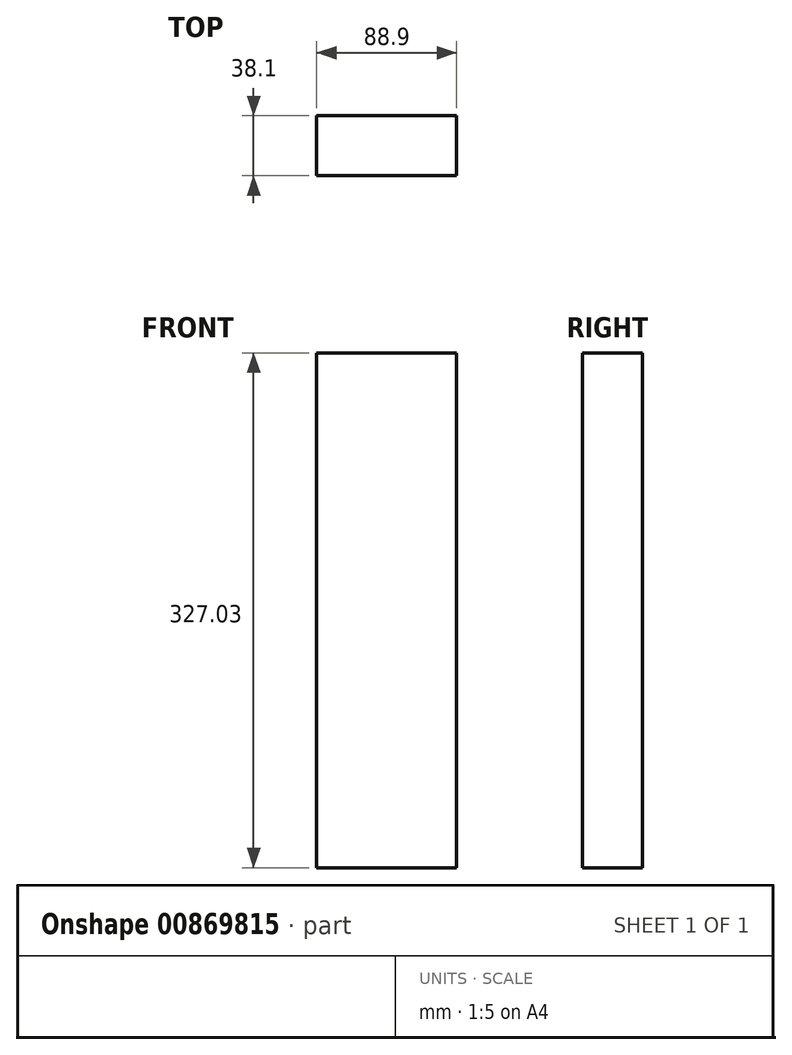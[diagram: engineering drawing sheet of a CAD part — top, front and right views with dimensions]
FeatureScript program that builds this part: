
annotation { "Feature Type Name" : "Feature", "Feature Type Description" : "" }
export const myFeature = defineFeature(function(context is Context, id is Id, definition is map)
    precondition{}
    {
        {
            var Q0;
            Q0=qCreatedBy(makeId("Top.planeOp"),FACE);
            var sketch = newSketch(context, id + "F0", { "sketchPlane" : qUnion([Q0])});
            skLineSegment(sketch, "E0.bottom", {"start": v(44.45, -19.05) * mm, "end": v(-44.45, -19.05) * mm});
            skLineSegment(sketch, "E0.top", {"start": v(44.45, 19.05) * mm, "end": v(-44.45, 19.05) * mm});
            skLineSegment(sketch, "E0.left", {"start": v(44.45, -19.05) * mm, "end": v(44.45, 19.05) * mm});
            skLineSegment(sketch, "E0.right", {"start": v(-44.45, -19.05) * mm, "end": v(-44.45, 19.05) * mm});
            skPoint(sketch, "E0.middle", {"position": v(0, 0) * mm});
            skSolve(sketch);
        }
        {
            var Q0;
            Q0=makeQuery(id+"F0.imprint","IMPRINT",FACE,{"disambiguationData":[TD([[makeQuery(id+"F0.imprint","IMPRINT",EDGE,{"derivedFrom":sQuery(id+"F0.wireOp",EDGE,"E0.bottom")}),-1.0]])]});
            extrude(context, id + "F1", {"entities" : qUnion([Q0]), "depth" : 327.02 * mm, "offsetDistance" : 25.4 * mm});
        }
    });
